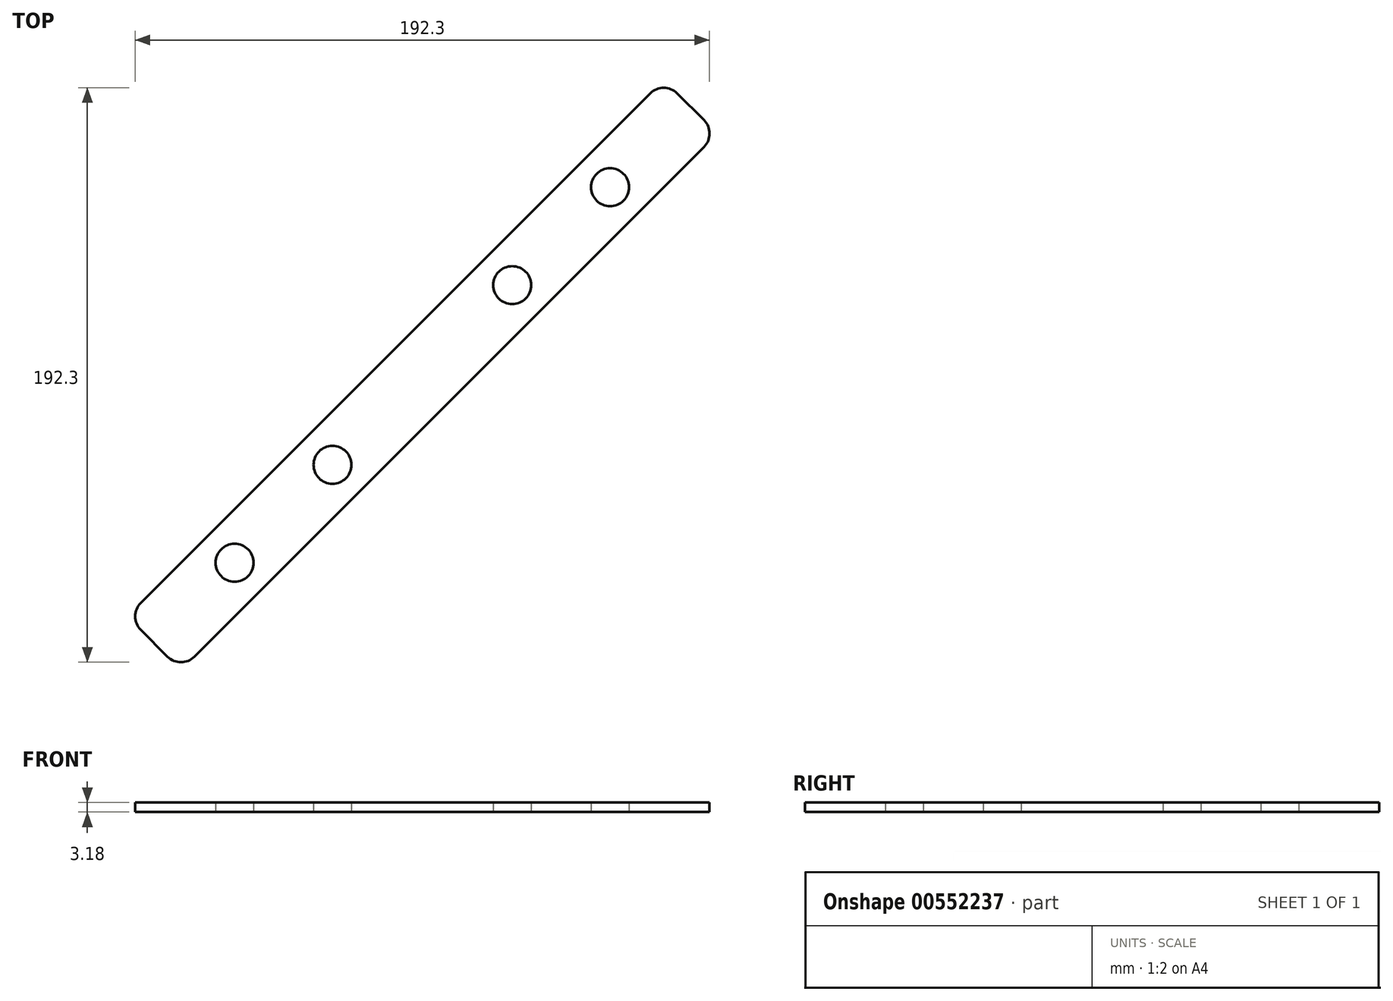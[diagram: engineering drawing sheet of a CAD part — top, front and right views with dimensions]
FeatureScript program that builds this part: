
annotation { "Feature Type Name" : "Feature", "Feature Type Description" : "" }
export const myFeature = defineFeature(function(context is Context, id is Id, definition is map)
    precondition{}
    {
        {
            var Q0;
            Q0=qCreatedBy(makeId("Top.planeOp"),FACE);
            var sketch = newSketch(context, id + "F0", { "sketchPlane" : qUnion([Q0])});
            skPoint(sketch, "E0.middle", {"position": v(0, 0) * mm});
            skLineSegment(sketch, "E1.top", {"start": v(-8.98, 8.98) * mm, "end": v(76.33, 94.3) * mm});
            skLineSegment(sketch, "E1.right", {"start": v(89.8, 89.8) * mm, "end": v(85.31, 94.3) * mm});
            skLineSegment(sketch, "E2.top", {"start": v(8.98, -8.98) * mm, "end": v(-76.33, -94.3) * mm});
            skLineSegment(sketch, "E2.right", {"start": v(-89.8, -89.8) * mm, "end": v(-85.31, -94.3) * mm});
            skCircle(sketch, "E3", {"center": v(-62.86, -62.86) * mm, "radius": 6.35 * mm});
            skCircle(sketch, "E4", {"center": v(-30.08, -30.08) * mm, "radius": 6.35 * mm});
            skCircle(sketch, "E5", {"center": v(30.08, 30.08) * mm, "radius": 6.35 * mm});
            skCircle(sketch, "E6", {"center": v(62.86, 62.86) * mm, "radius": 6.35 * mm});
            skArc(sketch, "E7.filletArc", {"start": v(-85.31, -94.3) * mm, "mid": v(-80.82, -96.15) * mm, "end": v(-76.33, -94.3) * mm});
            skArc(sketch, "E8.filletArc", {"start": v(-94.3, -76.33) * mm, "mid": v(-96.15, -80.82) * mm, "end": v(-94.3, -85.31) * mm});
            skArc(sketch, "E9.filletArc", {"start": v(94.3, 76.33) * mm, "mid": v(96.15, 80.82) * mm, "end": v(94.3, 85.31) * mm});
            skArc(sketch, "E10.filletArc", {"start": v(85.31, 94.3) * mm, "mid": v(80.82, 96.15) * mm, "end": v(76.33, 94.3) * mm});
            skLineSegment(sketch, "E11", {"start": v(-94.3, -85.31) * mm, "end": v(-89.8, -89.8) * mm});
            skLineSegment(sketch, "E12", {"start": v(-94.3, -76.33) * mm, "end": v(-8.98, 8.98) * mm});
            skLineSegment(sketch, "E13", {"start": v(8.98, -8.98) * mm, "end": v(94.3, 76.33) * mm});
            skLineSegment(sketch, "E14", {"start": v(94.3, 85.31) * mm, "end": v(89.8, 89.8) * mm});
            skSolve(sketch);
        }
        {
            var Q0;
            Q0=makeQuery(id+"F0.imprint","IMPRINT",FACE,{"disambiguationData":[TD([[makeQuery(id+"F0.imprint","IMPRINT",EDGE,{"derivedFrom":sQuery(id+"F0.wireOp",EDGE,"E1.top")}),-1.0]])]});
            extrude(context, id + "F1", {"entities" : qUnion([Q0]), "depth" : 3.17 * mm, "offsetDistance" : 25.4 * mm});
        }
    });
